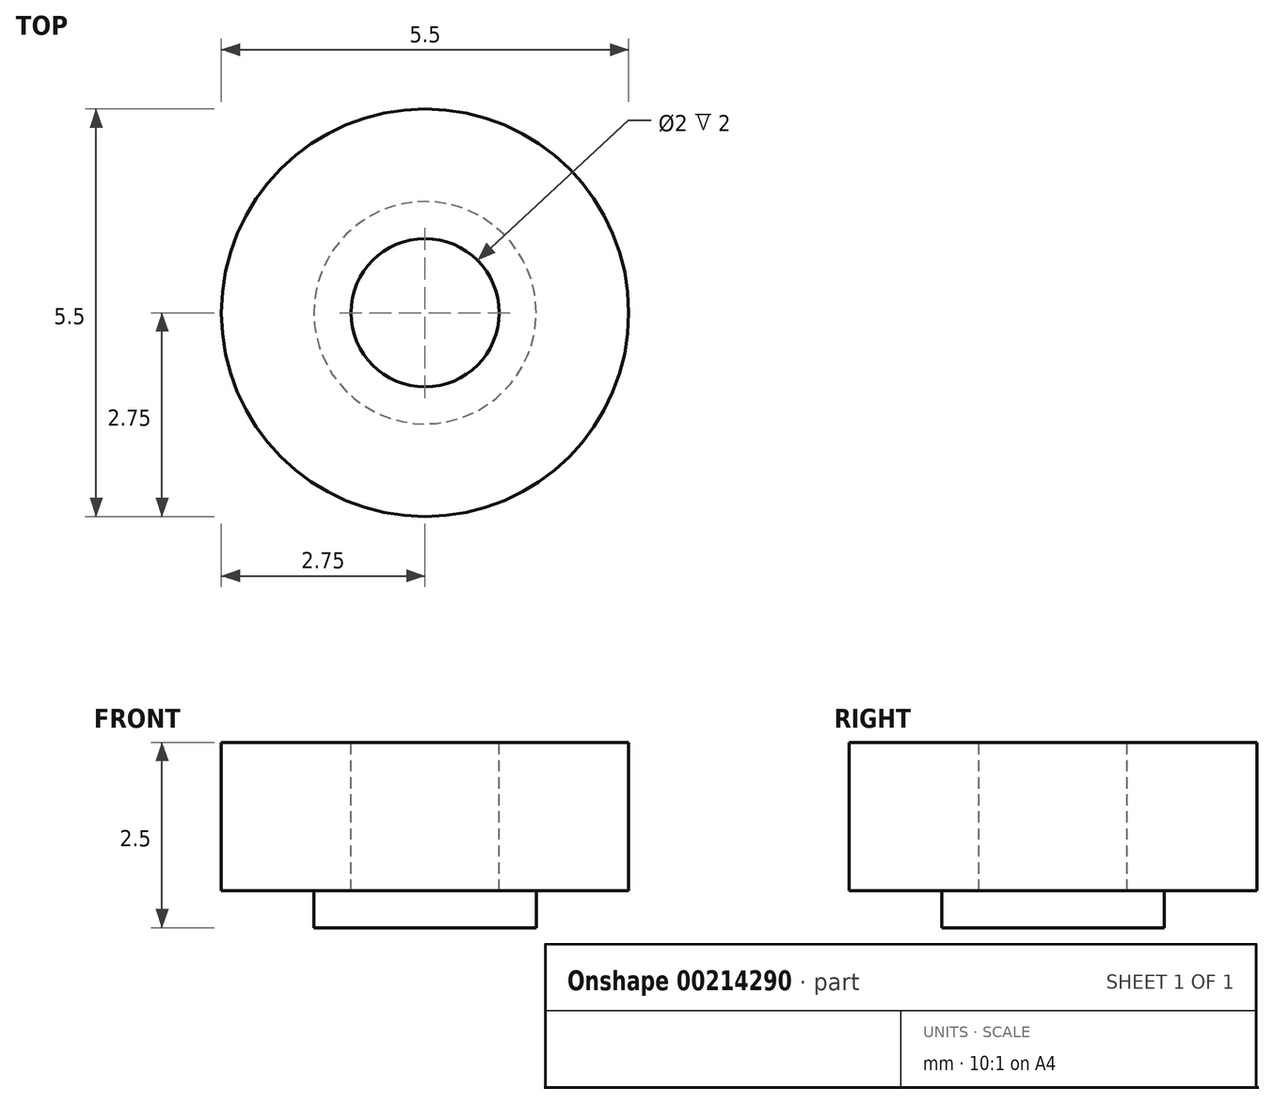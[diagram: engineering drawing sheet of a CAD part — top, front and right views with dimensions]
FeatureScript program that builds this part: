
annotation { "Feature Type Name" : "Feature", "Feature Type Description" : "" }
export const myFeature = defineFeature(function(context is Context, id is Id, definition is map)
    precondition{}
    {
        {
            var Q0;
            Q0=qCreatedBy(makeId("Top.planeOp"),FACE);
            var sketch = newSketch(context, id + "F0", { "sketchPlane" : qUnion([Q0])});
            skCircle(sketch, "E0", {"center": v(0, 0) * mm, "radius": 2.75 * mm});
            skSolve(sketch);
        }
        {
            var Q0;
            Q0=qSketchRegion(id+"F0",true);
            extrude(context, id + "F1", {"entities" : qUnion([Q0]), "depth" : 8 * mm});
        }
        {
            var Q0;
            Q0=makeQuery(id+"F1.opExtrude","CAP_FACE",FACE,{"disambiguationData":[OSD([sQuery(id+"F0.wireOp",EDGE,"E0")])],"isStart":true});
            var sketch = newSketch(context, id + "F2", { "sketchPlane" : qUnion([Q0])});
            skCircle(sketch, "E1", {"center": v(0, 0) * mm, "radius": 1.5 * mm});
            skCircle(sketch, "E2", {"center": v(0, 0) * mm, "radius": 2.75 * mm});
            skSolve(sketch);
        }
        {
            var Q0;
            Q0=qSketchRegion(id+"F2",true);
            extrude(context, id + "F3", {"entities" : qUnion([Q0]), "operationType" : NewBodyOperationType.REMOVE, "oppositeDirection" : true, "depth" : 6 * mm});
        }
        {
            var Q0;
            Q0=makeQuery(id+"F1.opExtrude","CAP_FACE",FACE,{"disambiguationData":[OSD([sQuery(id+"F0.wireOp",EDGE,"E0")])],"isStart":false});
            var sketch = newSketch(context, id + "F4", { "sketchPlane" : qUnion([Q0])});
            skCircle(sketch, "E3", {"center": v(0, 0) * mm, "radius": 1 * mm});
            skSolve(sketch);
        }
        {
            var Q0;
            Q0=qSketchRegion(id+"F4",true);
            extrude(context, id + "F5", {"entities" : qUnion([Q0]), "operationType" : NewBodyOperationType.REMOVE, "oppositeDirection" : true, "depth" : 2 * mm});
        }
        {
            var Q0;
            Q0=makeQuery(id+"F1.opExtrude","CAP_FACE",FACE,{"disambiguationData":[OSD([sQuery(id+"F0.wireOp",EDGE,"E0")])],"isStart":true});
            var sketch = newSketch(context, id + "F6", { "sketchPlane" : qUnion([Q0])});
            skCircle(sketch, "E4", {"center": v(0, 0) * mm, "radius": 1.5 * mm});
            skSolve(sketch);
        }
        {
            var Q0;
            Q0 = qSketchRegion(id + "F6", true);
            extrude(context, id + "F7", {"entities" : qUnion([Q0]), "operationType" : NewBodyOperationType.REMOVE, "oppositeDirection" : true, "depth" : 5.5 * mm});
        }
    });
